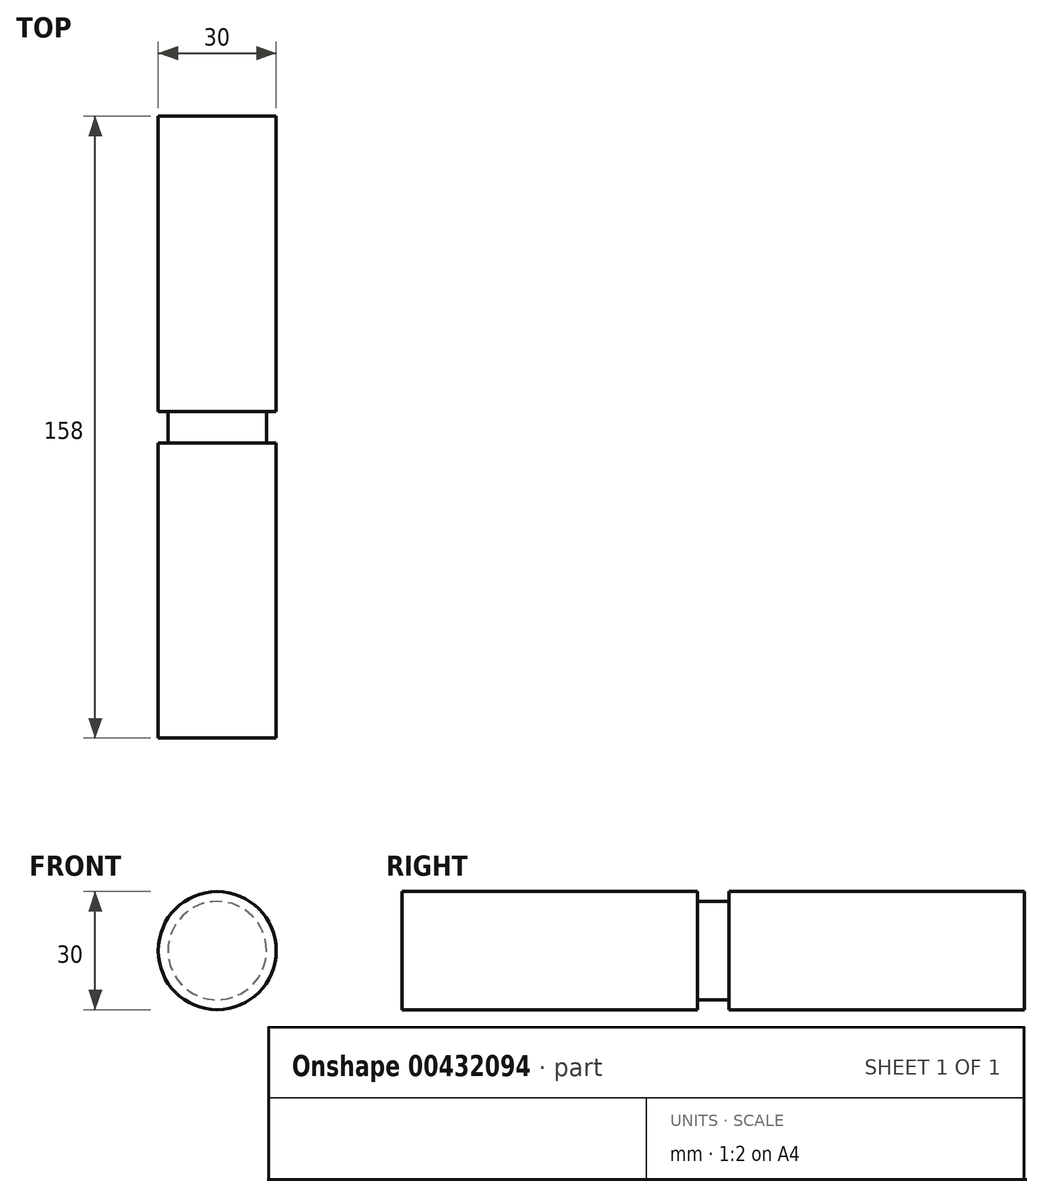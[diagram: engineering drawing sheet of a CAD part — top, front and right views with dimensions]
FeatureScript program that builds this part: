
annotation { "Feature Type Name" : "Feature", "Feature Type Description" : "" }
export const myFeature = defineFeature(function(context is Context, id is Id, definition is map)
    precondition{}
    {
        {
            var Q0;
            Q0=qCreatedBy(makeId("Front.planeOp"),FACE);
            var sketch = newSketch(context, id + "F0", { "sketchPlane" : qUnion([Q0])});
            skCircle(sketch, "E0", {"center": v(0, 0) * mm, "radius": 12.5 * mm});
            skSolve(sketch);
        }
        {
            var Q0;
            Q0 = qSketchRegion(id + "F0", true);
            extrude(context, id + "F1", {"entities" : qUnion([Q0]), "depth" : 4 * mm});
        }
        {
            var Q0;
            Q0=makeQuery(id+"F1.opExtrude","CAP_FACE",FACE,{"disambiguationData":[OSD([sQuery(id+"F0.wireOp",EDGE,"E0")])],"isStart":false});
            var sketch = newSketch(context, id + "F2", { "sketchPlane" : qUnion([Q0])});
            skCircle(sketch, "E1", {"center": v(0, 0) * mm, "radius": 15 * mm});
            skSolve(sketch);
        }
        {
            var Q0;
            Q0 = qSketchRegion(id + "F2", true);
            extrude(context, id + "F3", {"entities" : qUnion([Q0]), "operationType" : NewBodyOperationType.ADD, "depth" : 75 * mm});
        }
        {
            var Q0;
            Q0=makeQuery(id+"F1.opExtrude","SWEPT_BODY",BODY,{"disambiguationData":[OSD([sQuery(id+"F0.wireOp",EDGE,"E0")])]});
            var Q1;
            Q1=qCreatedBy(makeId("Front.planeOp"),FACE);
            mirror(context, id + "F4", {"operationType" : NewBodyOperationType.ADD, "entities" : qUnion([Q0]), "mirrorPlane" : qUnion([Q1])});
        }
    });
